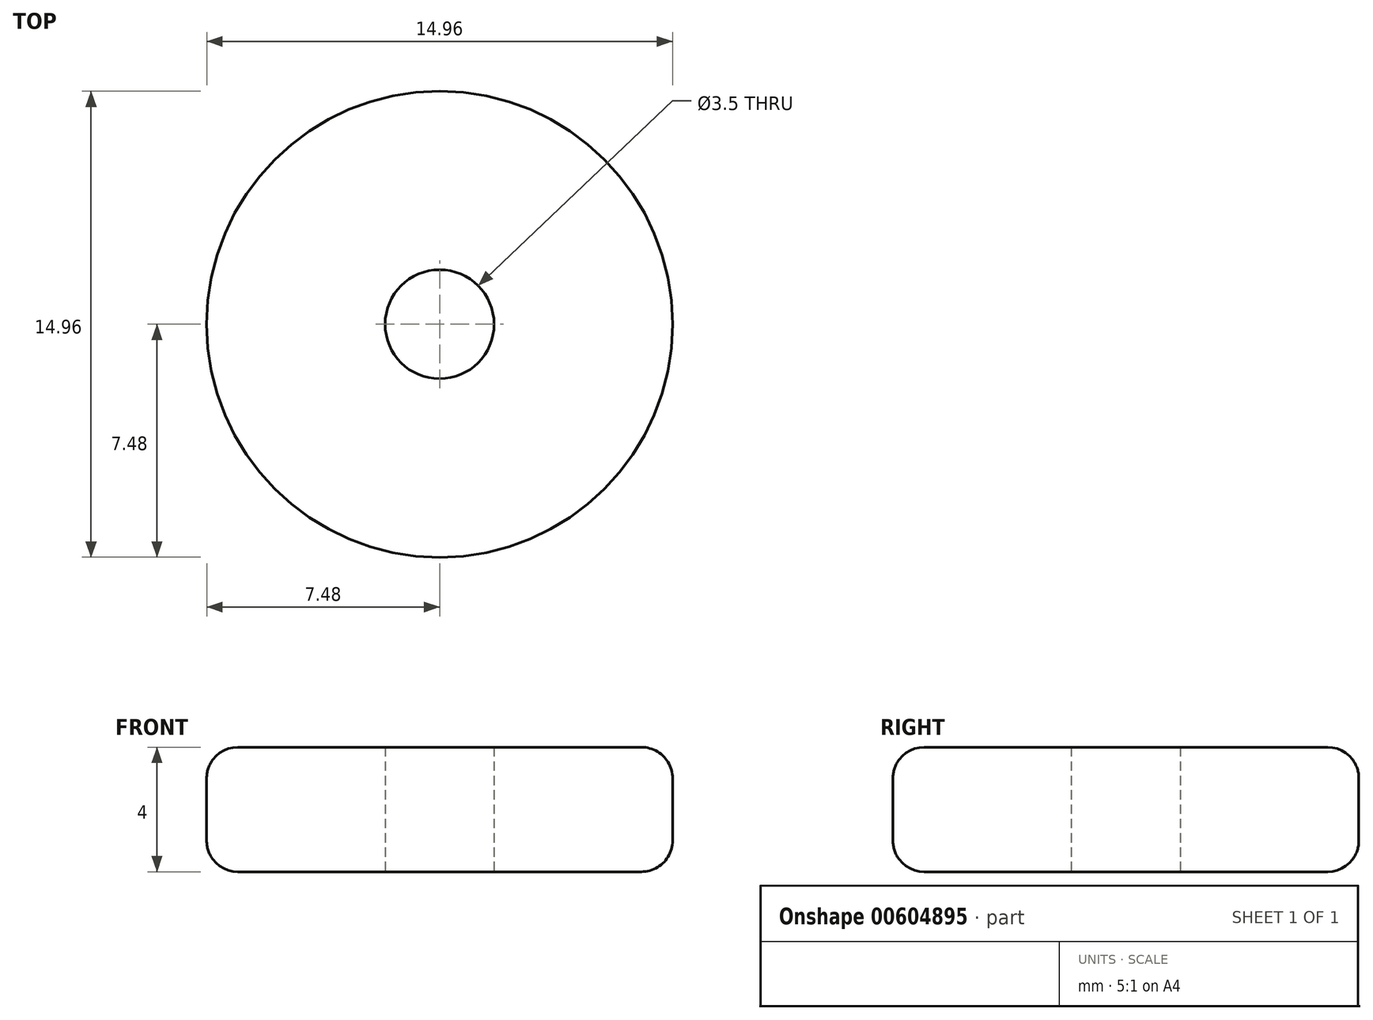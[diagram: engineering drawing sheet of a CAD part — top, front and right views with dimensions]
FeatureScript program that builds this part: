
annotation { "Feature Type Name" : "Feature", "Feature Type Description" : "" }
export const myFeature = defineFeature(function(context is Context, id is Id, definition is map)
    precondition{}
    {
        {
            var Q0;
            Q0=qCreatedBy(makeId("Top.planeOp"),FACE);
            var sketch = newSketch(context, id + "F0", { "sketchPlane" : qUnion([Q0])});
            skCircle(sketch, "E0", {"center": v(0, 0) * mm, "radius": 7.48 * mm});
            skCircle(sketch, "E1", {"center": v(0, 0) * mm, "radius": 1.75 * mm});
            skSolve(sketch);
        }
        {
            var Q0;
            Q0=makeQuery(id+"F0.imprint","IMPRINT",FACE,{"disambiguationData":[TD([[makeQuery(id+"F0.imprint","IMPRINT",EDGE,{"derivedFrom":sQuery(id+"F0.wireOp",EDGE,"E0")}),1.0]])]});
            extrude(context, id + "F1", {"entities" : qUnion([Q0]), "depth" : 4 * mm, "offsetDistance" : 25 * mm});
        }
        {
            var Q0;
            Q0=makeQuery(id+"F1.opExtrude","CAP_EDGE",EDGE,{"disambiguationData":[OSD([sQuery(id+"F0.wireOp",EDGE,"E0")])],"isStart":true});
            var Q1;
            Q1=makeQuery(id+"F1.opExtrude","CAP_EDGE",EDGE,{"disambiguationData":[OSD([sQuery(id+"F0.wireOp",EDGE,"E0")])],"isStart":false});
            fillet(context, id + "F2", {"entities" : qUnion([Q0, Q1]), "radius" : 1 * mm, "tangentPropagation" : true, "allowEdgeOverflow" : false});
        }
    });
